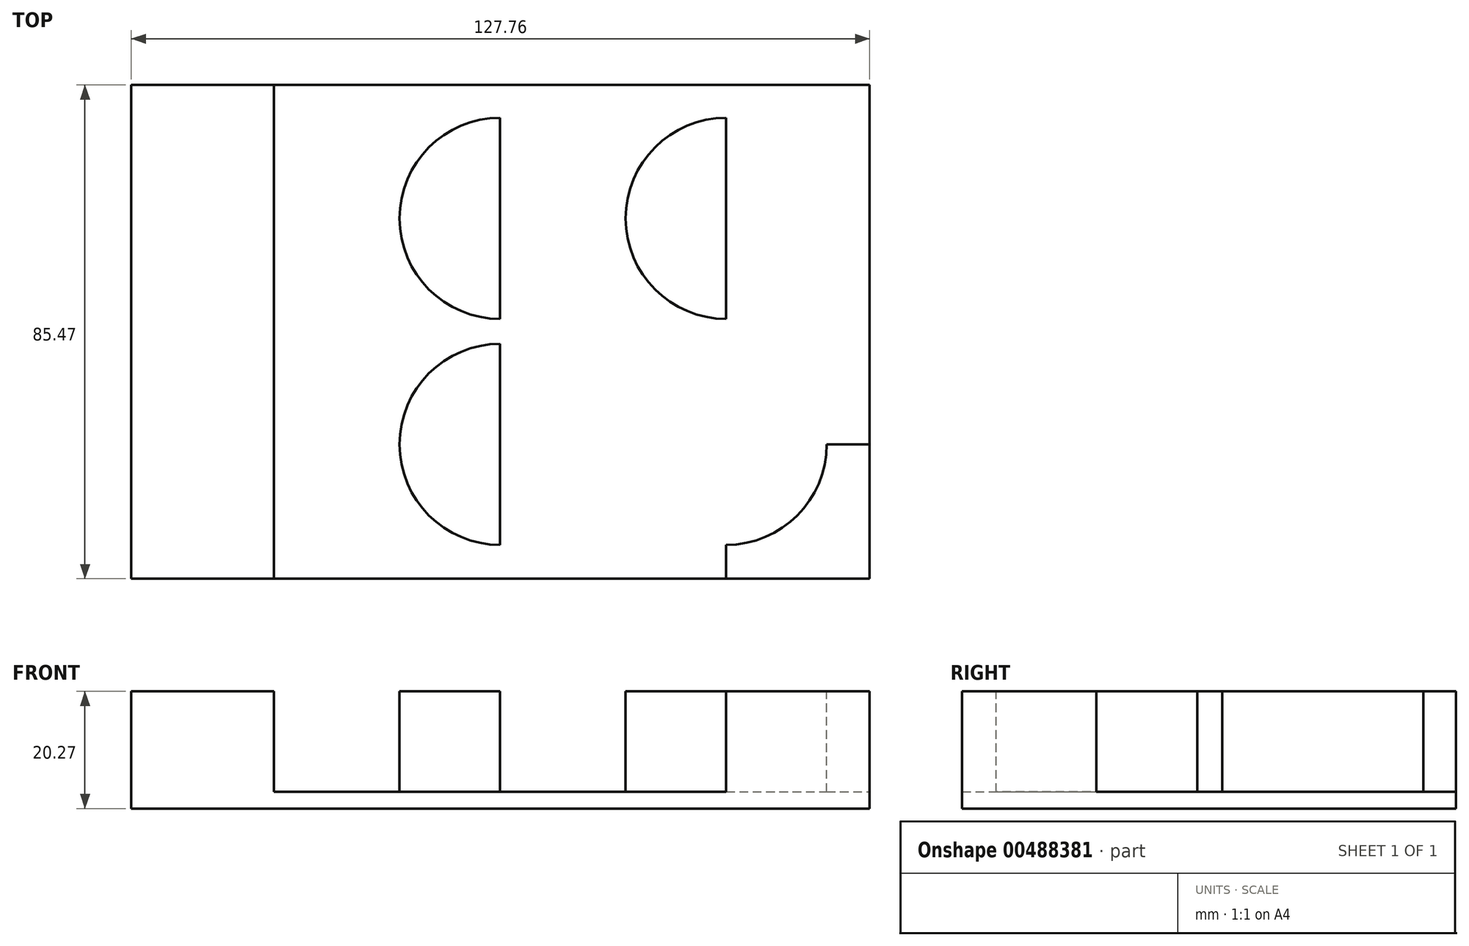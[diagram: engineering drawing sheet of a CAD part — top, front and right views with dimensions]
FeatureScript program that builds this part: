
annotation { "Feature Type Name" : "Feature", "Feature Type Description" : "" }
export const myFeature = defineFeature(function(context is Context, id is Id, definition is map)
    precondition{}
    {
        {
            var Q0;
            Q0=qCreatedBy(makeId("Top.planeOp"),FACE);
            var sketch = newSketch(context, id + "F0", { "sketchPlane" : qUnion([Q0])});
            skLineSegment(sketch, "E0.bottom", {"start": v(63.88, 42.73) * mm, "end": v(-63.88, 42.73) * mm});
            skLineSegment(sketch, "E0.top", {"start": v(63.88, -42.73) * mm, "end": v(-63.88, -42.73) * mm});
            skLineSegment(sketch, "E0.left", {"start": v(63.88, 42.74) * mm, "end": v(63.88, -42.73) * mm});
            skLineSegment(sketch, "E0.right", {"start": v(-63.88, 42.73) * mm, "end": v(-63.88, -42.73) * mm});
            skPoint(sketch, "E0.middle", {"position": v(0, 0) * mm});
            skSolve(sketch);
        }
        {
            var Q0;
            Q0=qSketchRegion(id+"F0",true);
            extrude(context, id + "F1", {"entities" : qUnion([Q0]), "depth" : 20.27 * mm});
        }
        {
            var Q0;
            Q0=makeQuery(id+"F1.opExtrude","CAP_FACE",FACE,{"disambiguationData":[OSD([sQuery(id+"F0.wireOp",EDGE,"E0.bottom"),sQuery(id+"F0.wireOp",EDGE,"E0.top"),sQuery(id+"F0.wireOp",EDGE,"E0.left"),sQuery(id+"F0.wireOp",EDGE,"E0.right")])],"isStart":false});
            var sketch = newSketch(context, id + "F2", { "sketchPlane" : qUnion([Q0])});
            skLineSegment(sketch, "E1.bottom", {"start": v(63.95, 42.8) * mm, "end": v(-63.95, 42.8) * mm});
            skLineSegment(sketch, "E1.top", {"start": v(63.95, -42.8) * mm, "end": v(-63.95, -42.8) * mm});
            skLineSegment(sketch, "E1.left", {"start": v(63.95, 42.8) * mm, "end": v(63.95, -42.8) * mm});
            skLineSegment(sketch, "E1.right", {"start": v(-63.95, 42.8) * mm, "end": v(-63.95, -42.8) * mm});
            skPoint(sketch, "E1.middle", {"position": v(0, 0) * mm});
            skLineSegment(sketch, "E2", {"start": v(-63.95, -42.8) * mm, "end": v(-39.19, -42.8) * mm});
            skLineSegment(sketch, "E3", {"start": v(-63.95, 42.8) * mm, "end": v(-63.95, 19.64) * mm});
            skLineSegment(sketch, "E4", {"start": v(-39.19, -42.8) * mm, "end": v(-0.07, -42.8) * mm});
            skLineSegment(sketch, "E5", {"start": v(-0.07, -42.8) * mm, "end": v(39.05, -42.8) * mm});
            skLineSegment(sketch, "E6", {"start": v(-63.95, 19.64) * mm, "end": v(-63.95, -19.48) * mm});
            skLineSegment(sketch, "E7", {"start": v(-63.95, 19.64) * mm, "end": v(63.95, 19.64) * mm});
            skLineSegment(sketch, "E8", {"start": v(63.95, 19.64) * mm, "end": v(63.95, 42.8) * mm});
            skLineSegment(sketch, "E9", {"start": v(-63.95, -19.48) * mm, "end": v(63.95, -19.48) * mm});
            skLineSegment(sketch, "E10", {"start": v(63.95, -19.48) * mm, "end": v(63.95, 19.64) * mm});
            skLineSegment(sketch, "E11", {"start": v(-39.19, -42.8) * mm, "end": v(-39.19, 42.8) * mm});
            skLineSegment(sketch, "E12", {"start": v(-39.19, 42.8) * mm, "end": v(-63.95, 42.8) * mm});
            skLineSegment(sketch, "E13", {"start": v(-0.07, -42.8) * mm, "end": v(-0.07, 42.8) * mm});
            skLineSegment(sketch, "E14", {"start": v(-0.07, 42.8) * mm, "end": v(-39.19, 42.8) * mm});
            skLineSegment(sketch, "E15", {"start": v(39.05, -42.8) * mm, "end": v(39.05, 42.8) * mm});
            skLineSegment(sketch, "E16", {"start": v(39.05, 42.8) * mm, "end": v(-0.07, 42.8) * mm});
            skCircle(sketch, "E17", {"center": v(-39.19, 19.64) * mm, "radius": 17.4 * mm});
            skCircle(sketch, "E18", {"center": v(-0.07, 19.64) * mm, "radius": 17.4 * mm});
            skCircle(sketch, "E19", {"center": v(39.05, 19.64) * mm, "radius": 17.4 * mm});
            skCircle(sketch, "E20", {"center": v(-0.07, -19.48) * mm, "radius": 17.4 * mm});
            skCircle(sketch, "E21", {"center": v(39.05, -19.48) * mm, "radius": 17.4 * mm});
            skCircle(sketch, "E22", {"center": v(-39.19, -19.48) * mm, "radius": 17.4 * mm});
            skSolve(sketch);
        }
        {
            var Q0;
            {var subQ0=sQuery(id+"F2.wireOp",EDGE,"E17");var subQ1=sQuery(id+"F2.wireOp",EDGE,"E7");var subQ2=makeQuery(id+"F2.imprint","INTERSECT",VERTEX,{"disambiguationData":[OD(0.0)],"derivedFrom":[subQ1,subQ0]});Q0=makeQuery(id+"F2.imprint","IMPRINT",FACE,{"disambiguationData":[TD([[makeQuery(id+"F2.imprint","IMPRINT",EDGE,{"disambiguationData":[TD([[subQ2,-1.0]])],"derivedFrom":subQ1}),1.0]])]});}
            var Q1;
            {var subQ0=sQuery(id+"F2.wireOp",EDGE,"E11");var subQ1=sQuery(id+"F2.wireOp",EDGE,"E7");var subQ2=makeQuery(id+"F2.imprint","INTERSECT",VERTEX,{"derivedFrom":[subQ1,subQ0]});Q1=makeQuery(id+"F2.imprint","IMPRINT",FACE,{"disambiguationData":[TD([[makeQuery(id+"F2.imprint","IMPRINT",EDGE,{"disambiguationData":[TD([[subQ2,-1.0]])],"derivedFrom":subQ1}),1.0]])]});}
            var Q2;
            {var subQ0=sQuery(id+"F2.wireOp",EDGE,"E11");var subQ1=sQuery(id+"F2.wireOp",EDGE,"E7");var subQ2=makeQuery(id+"F2.imprint","INTERSECT",VERTEX,{"derivedFrom":[subQ1,subQ0]});Q2=makeQuery(id+"F2.imprint","IMPRINT",FACE,{"disambiguationData":[TD([[makeQuery(id+"F2.imprint","IMPRINT",EDGE,{"disambiguationData":[TD([[subQ2,-1.0]])],"derivedFrom":subQ1}),-1.0]])]});}
            var Q3;
            {var subQ0=sQuery(id+"F2.wireOp",EDGE,"E17");var subQ1=sQuery(id+"F2.wireOp",EDGE,"E7");var subQ2=makeQuery(id+"F2.imprint","INTERSECT",VERTEX,{"disambiguationData":[OD(0.0)],"derivedFrom":[subQ1,subQ0]});Q3=makeQuery(id+"F2.imprint","IMPRINT",FACE,{"disambiguationData":[TD([[makeQuery(id+"F2.imprint","IMPRINT",EDGE,{"disambiguationData":[TD([[subQ2,-1.0]])],"derivedFrom":subQ1}),-1.0]])]});}
            var Q4;
            {var subQ0=sQuery(id+"F2.wireOp",EDGE,"E22");var subQ1=sQuery(id+"F2.wireOp",EDGE,"E9");var subQ2=makeQuery(id+"F2.imprint","INTERSECT",VERTEX,{"disambiguationData":[OD(0.0)],"derivedFrom":[subQ1,subQ0]});Q4=makeQuery(id+"F2.imprint","IMPRINT",FACE,{"disambiguationData":[TD([[makeQuery(id+"F2.imprint","IMPRINT",EDGE,{"disambiguationData":[TD([[subQ2,-1.0]])],"derivedFrom":subQ1}),1.0]])]});}
            var Q5;
            {var subQ0=sQuery(id+"F2.wireOp",EDGE,"E11");var subQ1=sQuery(id+"F2.wireOp",EDGE,"E9");var subQ2=makeQuery(id+"F2.imprint","INTERSECT",VERTEX,{"derivedFrom":[subQ1,subQ0]});Q5=makeQuery(id+"F2.imprint","IMPRINT",FACE,{"disambiguationData":[TD([[makeQuery(id+"F2.imprint","IMPRINT",EDGE,{"disambiguationData":[TD([[subQ2,-1.0]])],"derivedFrom":subQ1}),1.0]])]});}
            var Q6;
            {var subQ0=sQuery(id+"F2.wireOp",EDGE,"E22");var subQ1=sQuery(id+"F2.wireOp",EDGE,"E9");var subQ2=makeQuery(id+"F2.imprint","INTERSECT",VERTEX,{"disambiguationData":[OD(0.0)],"derivedFrom":[subQ1,subQ0]});Q6=makeQuery(id+"F2.imprint","IMPRINT",FACE,{"disambiguationData":[TD([[makeQuery(id+"F2.imprint","IMPRINT",EDGE,{"disambiguationData":[TD([[subQ2,-1.0]])],"derivedFrom":subQ1}),-1.0]])]});}
            var Q7;
            {var subQ0=sQuery(id+"F2.wireOp",EDGE,"E11");var subQ1=sQuery(id+"F2.wireOp",EDGE,"E9");var subQ2=makeQuery(id+"F2.imprint","INTERSECT",VERTEX,{"derivedFrom":[subQ1,subQ0]});Q7=makeQuery(id+"F2.imprint","IMPRINT",FACE,{"disambiguationData":[TD([[makeQuery(id+"F2.imprint","IMPRINT",EDGE,{"disambiguationData":[TD([[subQ2,-1.0]])],"derivedFrom":subQ1}),-1.0]])]});}
            var Q8;
            {var subQ0=sQuery(id+"F2.wireOp",EDGE,"E18");var subQ1=sQuery(id+"F2.wireOp",EDGE,"E7");var subQ2=makeQuery(id+"F2.imprint","INTERSECT",VERTEX,{"disambiguationData":[OD(0.0)],"derivedFrom":[subQ1,subQ0]});Q8=makeQuery(id+"F2.imprint","IMPRINT",FACE,{"disambiguationData":[TD([[makeQuery(id+"F2.imprint","IMPRINT",EDGE,{"disambiguationData":[TD([[subQ2,-1.0]])],"derivedFrom":subQ1}),-1.0]])]});}
            var Q9;
            {var subQ0=sQuery(id+"F2.wireOp",EDGE,"E18");var subQ1=sQuery(id+"F2.wireOp",EDGE,"E7");var subQ2=makeQuery(id+"F2.imprint","INTERSECT",VERTEX,{"disambiguationData":[OD(0.0)],"derivedFrom":[subQ1,subQ0]});Q9=makeQuery(id+"F2.imprint","IMPRINT",FACE,{"disambiguationData":[TD([[makeQuery(id+"F2.imprint","IMPRINT",EDGE,{"disambiguationData":[TD([[subQ2,-1.0]])],"derivedFrom":subQ1}),1.0]])]});}
            var Q10;
            {var subQ0=sQuery(id+"F2.wireOp",EDGE,"E13");var subQ1=sQuery(id+"F2.wireOp",EDGE,"E7");var subQ2=makeQuery(id+"F2.imprint","INTERSECT",VERTEX,{"derivedFrom":[subQ1,subQ0]});Q10=makeQuery(id+"F2.imprint","IMPRINT",FACE,{"disambiguationData":[TD([[makeQuery(id+"F2.imprint","IMPRINT",EDGE,{"disambiguationData":[TD([[subQ2,-1.0]])],"derivedFrom":subQ1}),1.0]])]});}
            var Q11;
            {var subQ0=sQuery(id+"F2.wireOp",EDGE,"E13");var subQ1=sQuery(id+"F2.wireOp",EDGE,"E7");var subQ2=makeQuery(id+"F2.imprint","INTERSECT",VERTEX,{"derivedFrom":[subQ1,subQ0]});Q11=makeQuery(id+"F2.imprint","IMPRINT",FACE,{"disambiguationData":[TD([[makeQuery(id+"F2.imprint","IMPRINT",EDGE,{"disambiguationData":[TD([[subQ2,-1.0]])],"derivedFrom":subQ1}),-1.0]])]});}
            var Q12;
            {var subQ0=sQuery(id+"F2.wireOp",EDGE,"E13");var subQ1=sQuery(id+"F2.wireOp",EDGE,"E9");var subQ2=makeQuery(id+"F2.imprint","INTERSECT",VERTEX,{"derivedFrom":[subQ1,subQ0]});Q12=makeQuery(id+"F2.imprint","IMPRINT",FACE,{"disambiguationData":[TD([[makeQuery(id+"F2.imprint","IMPRINT",EDGE,{"disambiguationData":[TD([[subQ2,-1.0]])],"derivedFrom":subQ1}),1.0]])]});}
            var Q13;
            {var subQ0=sQuery(id+"F2.wireOp",EDGE,"E20");var subQ1=sQuery(id+"F2.wireOp",EDGE,"E9");var subQ2=makeQuery(id+"F2.imprint","INTERSECT",VERTEX,{"disambiguationData":[OD(0.0)],"derivedFrom":[subQ1,subQ0]});Q13=makeQuery(id+"F2.imprint","IMPRINT",FACE,{"disambiguationData":[TD([[makeQuery(id+"F2.imprint","IMPRINT",EDGE,{"disambiguationData":[TD([[subQ2,-1.0]])],"derivedFrom":subQ1}),1.0]])]});}
            var Q14;
            {var subQ0=sQuery(id+"F2.wireOp",EDGE,"E20");var subQ1=sQuery(id+"F2.wireOp",EDGE,"E9");var subQ2=makeQuery(id+"F2.imprint","INTERSECT",VERTEX,{"disambiguationData":[OD(0.0)],"derivedFrom":[subQ1,subQ0]});Q14=makeQuery(id+"F2.imprint","IMPRINT",FACE,{"disambiguationData":[TD([[makeQuery(id+"F2.imprint","IMPRINT",EDGE,{"disambiguationData":[TD([[subQ2,-1.0]])],"derivedFrom":subQ1}),-1.0]])]});}
            var Q15;
            {var subQ0=sQuery(id+"F2.wireOp",EDGE,"E13");var subQ1=sQuery(id+"F2.wireOp",EDGE,"E9");var subQ2=makeQuery(id+"F2.imprint","INTERSECT",VERTEX,{"derivedFrom":[subQ1,subQ0]});Q15=makeQuery(id+"F2.imprint","IMPRINT",FACE,{"disambiguationData":[TD([[makeQuery(id+"F2.imprint","IMPRINT",EDGE,{"disambiguationData":[TD([[subQ2,-1.0]])],"derivedFrom":subQ1}),-1.0]])]});}
            var Q16;
            {var subQ0=sQuery(id+"F2.wireOp",EDGE,"E21");var subQ1=sQuery(id+"F2.wireOp",EDGE,"E9");var subQ2=makeQuery(id+"F2.imprint","INTERSECT",VERTEX,{"disambiguationData":[OD(0.0)],"derivedFrom":[subQ1,subQ0]});Q16=makeQuery(id+"F2.imprint","IMPRINT",FACE,{"disambiguationData":[TD([[makeQuery(id+"F2.imprint","IMPRINT",EDGE,{"disambiguationData":[TD([[subQ2,-1.0]])],"derivedFrom":subQ1}),-1.0]])]});}
            var Q17;
            {var subQ0=sQuery(id+"F2.wireOp",EDGE,"E21");var subQ1=sQuery(id+"F2.wireOp",EDGE,"E9");var subQ2=makeQuery(id+"F2.imprint","INTERSECT",VERTEX,{"disambiguationData":[OD(0.0)],"derivedFrom":[subQ1,subQ0]});Q17=makeQuery(id+"F2.imprint","IMPRINT",FACE,{"disambiguationData":[TD([[makeQuery(id+"F2.imprint","IMPRINT",EDGE,{"disambiguationData":[TD([[subQ2,-1.0]])],"derivedFrom":subQ1}),1.0]])]});}
            var Q18;
            {var subQ0=sQuery(id+"F2.wireOp",EDGE,"E15");var subQ1=sQuery(id+"F2.wireOp",EDGE,"E9");var subQ2=makeQuery(id+"F2.imprint","INTERSECT",VERTEX,{"derivedFrom":[subQ1,subQ0]});Q18=makeQuery(id+"F2.imprint","IMPRINT",FACE,{"disambiguationData":[TD([[makeQuery(id+"F2.imprint","IMPRINT",EDGE,{"disambiguationData":[TD([[subQ2,-1.0]])],"derivedFrom":subQ1}),1.0]])]});}
            var Q19;
            {var subQ0=sQuery(id+"F2.wireOp",EDGE,"E15");var subQ1=sQuery(id+"F2.wireOp",EDGE,"E9");var subQ2=makeQuery(id+"F2.imprint","INTERSECT",VERTEX,{"derivedFrom":[subQ1,subQ0]});Q19=makeQuery(id+"F2.imprint","IMPRINT",FACE,{"disambiguationData":[TD([[makeQuery(id+"F2.imprint","IMPRINT",EDGE,{"disambiguationData":[TD([[subQ2,-1.0]])],"derivedFrom":subQ1}),-1.0]])]});}
            var Q20;
            {var subQ0=sQuery(id+"F2.wireOp",EDGE,"E15");var subQ1=sQuery(id+"F2.wireOp",EDGE,"E7");var subQ2=makeQuery(id+"F2.imprint","INTERSECT",VERTEX,{"derivedFrom":[subQ1,subQ0]});Q20=makeQuery(id+"F2.imprint","IMPRINT",FACE,{"disambiguationData":[TD([[makeQuery(id+"F2.imprint","IMPRINT",EDGE,{"disambiguationData":[TD([[subQ2,-1.0]])],"derivedFrom":subQ1}),-1.0]])]});}
            var Q21;
            {var subQ0=sQuery(id+"F2.wireOp",EDGE,"E19");var subQ1=sQuery(id+"F2.wireOp",EDGE,"E7");var subQ2=makeQuery(id+"F2.imprint","INTERSECT",VERTEX,{"disambiguationData":[OD(0.0)],"derivedFrom":[subQ1,subQ0]});Q21=makeQuery(id+"F2.imprint","IMPRINT",FACE,{"disambiguationData":[TD([[makeQuery(id+"F2.imprint","IMPRINT",EDGE,{"disambiguationData":[TD([[subQ2,-1.0]])],"derivedFrom":subQ1}),1.0]])]});}
            var Q22;
            {var subQ0=sQuery(id+"F2.wireOp",EDGE,"E15");var subQ1=sQuery(id+"F2.wireOp",EDGE,"E7");var subQ2=makeQuery(id+"F2.imprint","INTERSECT",VERTEX,{"derivedFrom":[subQ1,subQ0]});Q22=makeQuery(id+"F2.imprint","IMPRINT",FACE,{"disambiguationData":[TD([[makeQuery(id+"F2.imprint","IMPRINT",EDGE,{"disambiguationData":[TD([[subQ2,-1.0]])],"derivedFrom":subQ1}),1.0]])]});}
            var Q23;
            {var subQ0=sQuery(id+"F2.wireOp",EDGE,"E19");var subQ1=sQuery(id+"F2.wireOp",EDGE,"E7");var subQ2=makeQuery(id+"F2.imprint","INTERSECT",VERTEX,{"disambiguationData":[OD(0.0)],"derivedFrom":[subQ1,subQ0]});Q23=makeQuery(id+"F2.imprint","IMPRINT",FACE,{"disambiguationData":[TD([[makeQuery(id+"F2.imprint","IMPRINT",EDGE,{"disambiguationData":[TD([[subQ2,-1.0]])],"derivedFrom":subQ1}),-1.0]])]});}
            extrude(context, id + "F3", {"entities" : qUnion([Q0, Q1, Q2, Q3, Q4, Q5, Q6, Q7, Q8, Q9, Q10, Q11, Q12, Q13, Q14, Q15, Q16, Q17, Q18, Q19, Q20, Q21, Q22, Q23]), "operationType" : NewBodyOperationType.REMOVE, "oppositeDirection" : true, "depth" : 17.4 * mm});
        }
    });
